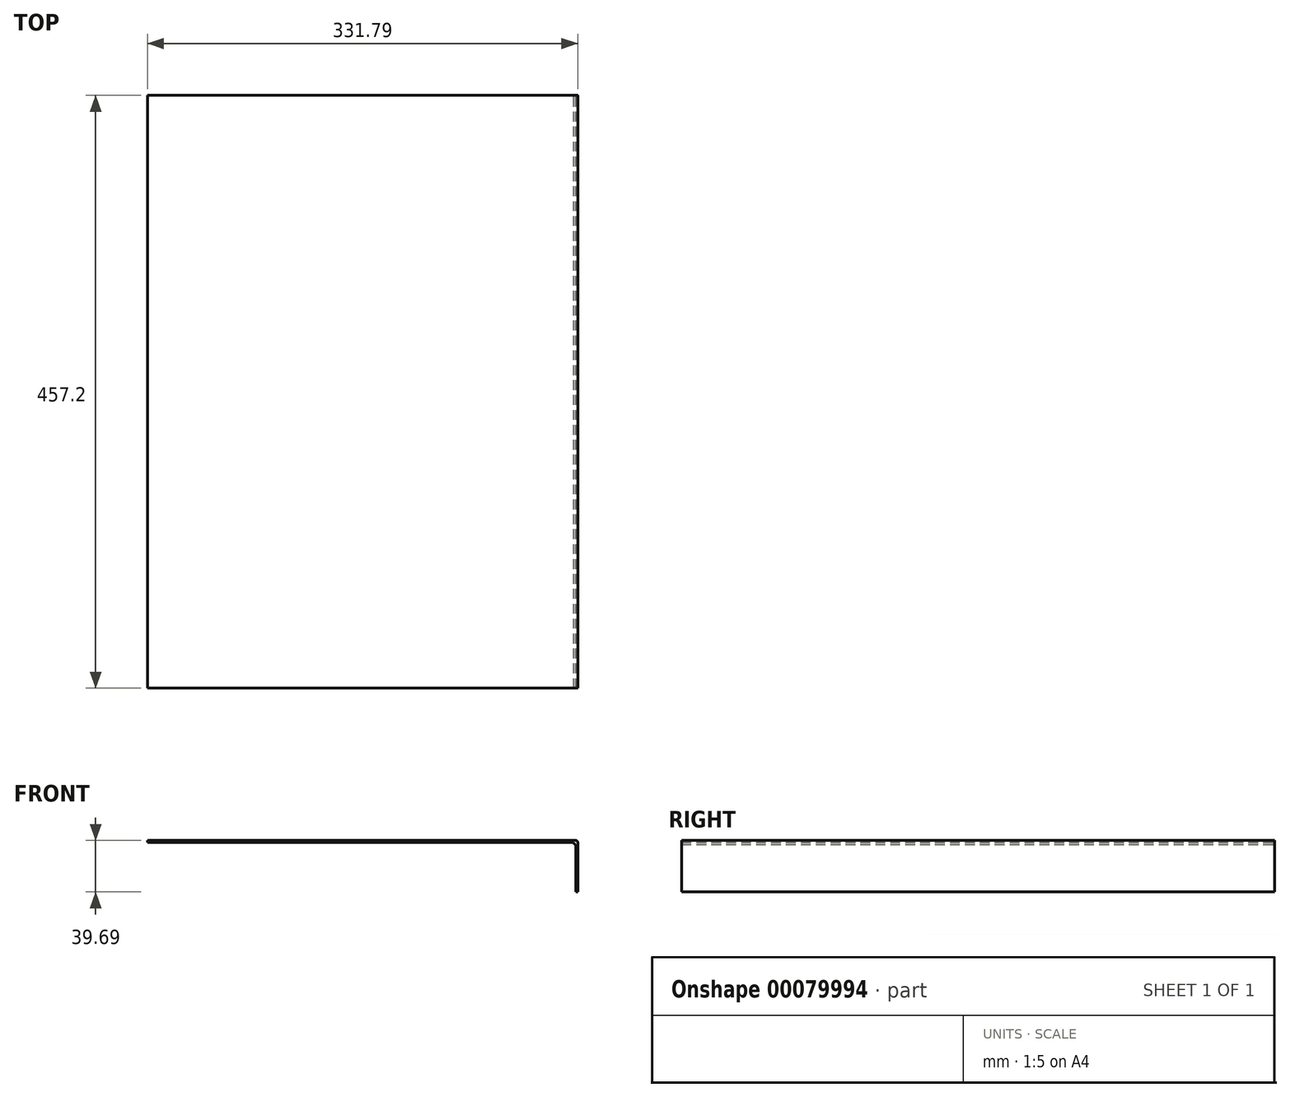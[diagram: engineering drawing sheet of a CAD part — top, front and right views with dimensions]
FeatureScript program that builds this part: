
annotation { "Feature Type Name" : "Feature", "Feature Type Description" : "" }
export const myFeature = defineFeature(function(context is Context, id is Id, definition is map)
    precondition{}
    {
        {
            var Q0;
            Q0=qCreatedBy(makeId("Front.planeOp"),FACE);
            var sketch = newSketch(context, id + "F0", { "sketchPlane" : qUnion([Q0])});
            skCircle(sketch, "E0", {"center": v(0, 0) * mm, "radius": 1.59 * mm});
            skLineSegment(sketch, "E1", {"start": v(0, 1.59) * mm, "end": v(-330.2, 1.59) * mm});
            skLineSegment(sketch, "E2", {"start": v(-330.2, 1.59) * mm, "end": v(-330.2, 0) * mm});
            skLineSegment(sketch, "E3", {"start": v(-330.2, 0) * mm, "end": v(-1.59, 0) * mm});
            skLineSegment(sketch, "E4", {"start": v(1.59, 0) * mm, "end": v(1.59, -38.1) * mm});
            skLineSegment(sketch, "E5", {"start": v(1.59, -38.1) * mm, "end": v(0, -38.1) * mm});
            skLineSegment(sketch, "E6", {"start": v(0, -38.1) * mm, "end": v(0, -1.59) * mm});
            skSolve(sketch);
        }
        {
            var Q0;
            {var subQ0=sQuery(id+"F0.wireOp",EDGE,"E1");Q0=makeQuery(id+"F0.imprint","IMPRINT",FACE,{"disambiguationData":[TD([[makeQuery(id+"F0.imprint","IMPRINT",EDGE,{"derivedFrom":subQ0}),1.0]])]});}
            var Q1;
            {var subQ0=sQuery(id+"F0.wireOp",EDGE,"E4");Q1=makeQuery(id+"F0.imprint","IMPRINT",FACE,{"disambiguationData":[TD([[makeQuery(id+"F0.imprint","IMPRINT",EDGE,{"derivedFrom":subQ0}),-1.0]])]});}
            var Q2;
            {var subQ0=sQuery(id+"F0.wireOp",EDGE,"E0");var subQ1=makeQuery(id+"F0.imprint","INTERSECT",VERTEX,{"derivedFrom":[subQ0,sQuery(id+"F0.wireOp",EDGE,"E1")]});Q2=makeQuery(id+"F0.imprint","IMPRINT",FACE,{"disambiguationData":[TD([[makeQuery(id+"F0.imprint","IMPRINT",EDGE,{"disambiguationData":[TD([[subQ1,1.0]])],"derivedFrom":subQ0}),1.0]])]});}
            extrude(context, id + "F1", {"entities" : qUnion([Q0, Q1, Q2]), "endBound" : BoundingType.SYMMETRIC, "depth" : 457.2 * mm});
        }
    });
